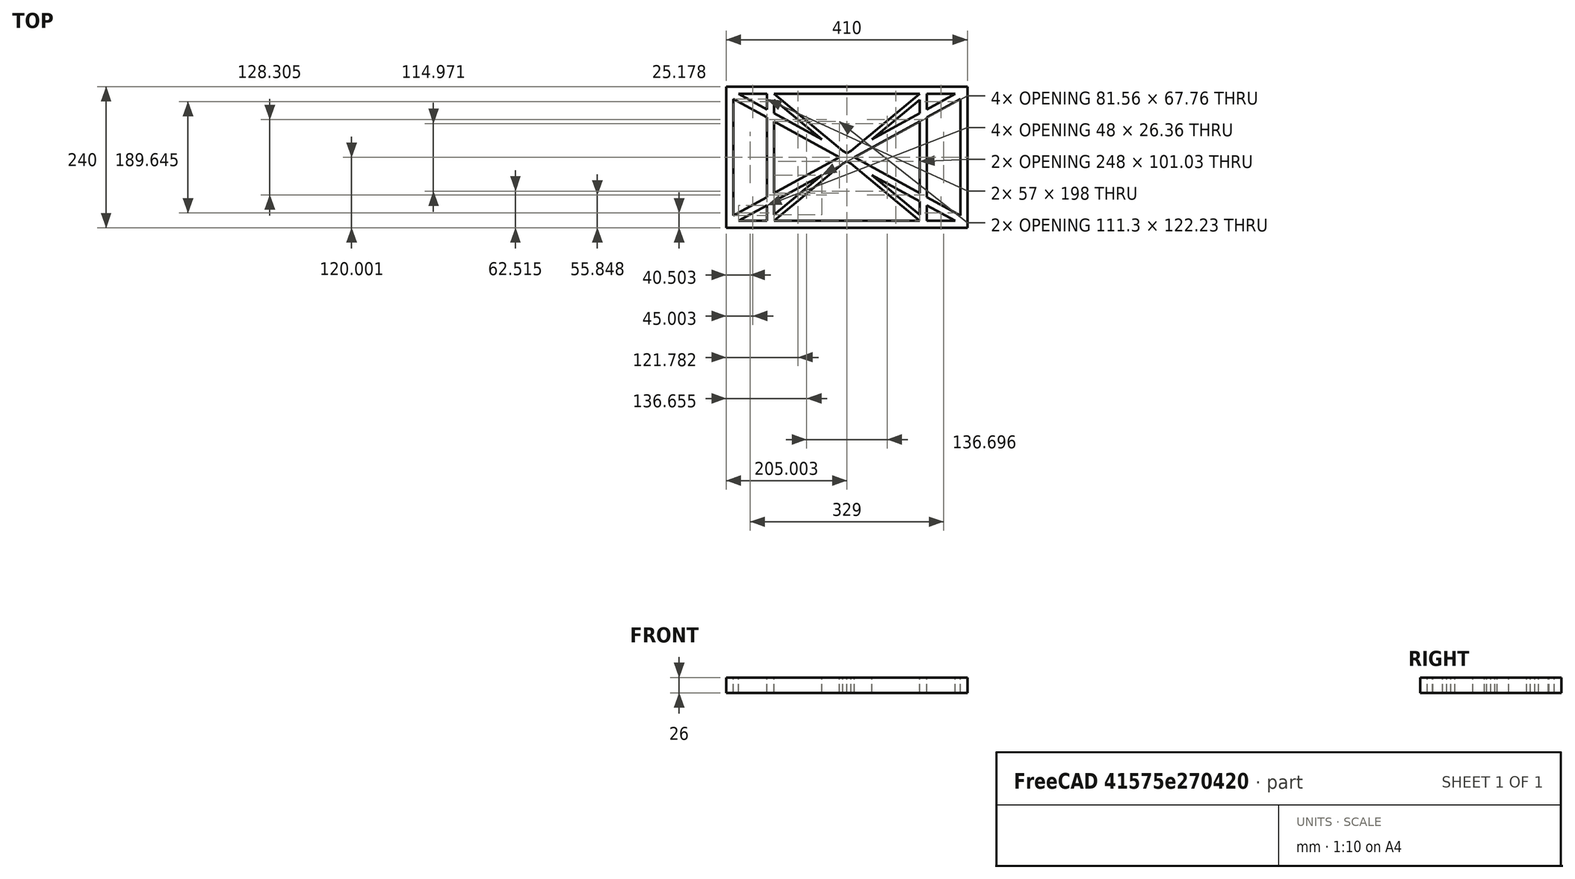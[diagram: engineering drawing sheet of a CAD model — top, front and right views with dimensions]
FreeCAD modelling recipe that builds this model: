
FCSTD DOCUMENT  (FreeCAD 0.19R0.19.2)
Label: laptopStand033
License: All rights reserved
LicenseURL: http://en.wikipedia.org/wiki/All_rights_reserved
objects: Sketcher::SketchObject×3, Part::Extrusion×1
note: 4 computed .brp shape members not serialized (recipe doc carries the construction recipe); baked Part::Feature solids carry a one-line shape summary decoded from their .brp

FEATURE [Sketcher::SketchObject] Sketch
  FullyConstrained = true
  sketch-geometry (52):
    g0: LineSegment StartX=-22.9272 StartY=136.221 StartZ=0 EndX=-22.9272 EndY=-103.779 EndZ=0
    g1: LineSegment StartX=-22.9272 StartY=136.221 StartZ=0 EndX=387.073 EndY=136.221 EndZ=0
    g2: LineSegment StartX=-22.9272 StartY=-103.779 StartZ=0 EndX=387.073 EndY=-103.779 EndZ=0
    g3: LineSegment StartX=387.073 StartY=136.221 StartZ=0 EndX=387.073 EndY=-103.779 EndZ=0
    g4: LineSegment StartX=375.073 StartY=115.221 StartZ=0 EndX=318.073 EndY=83.9235 EndZ=0
    g5: LineSegment StartX=-10.9272 StartY=-82.7794 StartZ=0 EndX=46.0728 EndY=-51.4823 EndZ=0
    g6: LineSegment StartX=-1.92719 StartY=124.221 StartZ=0 EndX=46.0728 EndY=97.8651 EndZ=0
    g7: LineSegment StartX=366.073 StartY=-91.7794 StartZ=0 EndX=318.073 EndY=-65.424 EndZ=0
    g8: LineSegment StartX=-10.9272 StartY=115.221 StartZ=0 EndX=-10.9272 EndY=-82.7794 EndZ=0
    g9: LineSegment StartX=375.073 StartY=-82.7794 StartZ=0 EndX=375.073 EndY=115.221 EndZ=0
    g10: LineSegment StartX=-1.92719 StartY=-91.7794 StartZ=0 EndX=46.0728 EndY=-91.7794 EndZ=0
    g11: LineSegment StartX=318.073 StartY=124.221 StartZ=0 EndX=366.073 EndY=124.221 EndZ=0
    g12: LineSegment StartX=306.073 StartY=-81.8102 StartZ=0 EndX=224.513 EndY=-14.0532 EndZ=0
    g13: LineSegment StartX=58.0728 StartY=114.251 StartZ=0 EndX=139.632 EndY=46.4944 EndZ=0
    g14: LineSegment StartX=306.073 StartY=124.221 StartZ=0 EndX=189.124 EndY=27.0628 EndZ=0
    g15: LineSegment StartX=58.0728 StartY=-91.7794 StartZ=0 EndX=175.022 EndY=5.37834 EndZ=0
    g16: LineSegment StartX=46.0728 StartY=124.221 StartZ=0 EndX=46.0728 EndY=97.8651 EndZ=0
    g17: LineSegment StartX=58.0728 StartY=-81.8102 StartZ=0 EndX=58.0728 EndY=-58.8351 EndZ=0
    g18: LineSegment StartX=318.073 StartY=124.221 StartZ=0 EndX=318.073 EndY=97.8651 EndZ=0
    g19: LineSegment StartX=306.073 StartY=114.251 StartZ=0 EndX=306.073 EndY=91.2763 EndZ=0
    g20: LineSegment StartX=182.073 StartY=23.1914 StartZ=0 EndX=189.124 EndY=27.0628 EndZ=0
    g21: LineSegment StartX=182.073 StartY=9.24976 StartZ=0 EndX=175.022 EndY=5.37834 EndZ=0
    g22: LineSegment StartX=224.513 StartY=46.4944 StartZ=0 EndX=306.073 EndY=114.251 EndZ=0
    g23: LineSegment StartX=175.022 StartY=27.0628 StartZ=0 EndX=58.0728 EndY=124.221 EndZ=0
    g24: LineSegment StartX=169.377 StartY=16.2206 StartZ=0 EndX=58.0728 EndY=77.3346 EndZ=0
    g25: LineSegment StartX=139.632 StartY=-14.0532 StartZ=0 EndX=58.0728 EndY=-81.8102 EndZ=0
    g26: LineSegment StartX=194.768 StartY=16.2206 StartZ=0 EndX=306.073 EndY=-44.8935 EndZ=0
    g27: LineSegment StartX=224.513 StartY=46.4944 StartZ=0 EndX=306.073 EndY=91.2763 EndZ=0
    g28: LineSegment StartX=175.022 StartY=27.0628 StartZ=0 EndX=182.073 EndY=23.1914 EndZ=0
    g29: LineSegment StartX=139.632 StartY=-14.0532 StartZ=0 EndX=58.0728 EndY=-58.8351 EndZ=0
    g30: LineSegment StartX=189.124 StartY=5.37834 StartZ=0 EndX=182.073 EndY=9.24976 EndZ=0
    g31: LineSegment StartX=189.124 StartY=5.37834 StartZ=0 EndX=306.073 EndY=-91.7794 EndZ=0
    g32: LineSegment StartX=306.073 StartY=77.3346 StartZ=0 EndX=306.073 EndY=-44.8935 EndZ=0
    g33: LineSegment StartX=318.073 StartY=83.9235 StartZ=0 EndX=318.073 EndY=-51.4823 EndZ=0
    g34: LineSegment StartX=318.073 StartY=97.8651 StartZ=0 EndX=366.073 EndY=124.221 EndZ=0
    g35: LineSegment StartX=306.073 StartY=77.3346 StartZ=0 EndX=194.768 EndY=16.2206 EndZ=0
    g36: LineSegment StartX=306.073 StartY=-58.8351 StartZ=0 EndX=224.513 EndY=-14.0532 EndZ=0
    g37: LineSegment StartX=306.073 StartY=-58.8351 StartZ=0 EndX=306.073 EndY=-81.8102 EndZ=0
    g38: LineSegment StartX=318.073 StartY=-51.4823 StartZ=0 EndX=375.073 EndY=-82.7794 EndZ=0
    g39: LineSegment StartX=318.073 StartY=-65.424 StartZ=0 EndX=318.073 EndY=-91.7794 EndZ=0
    g40: LineSegment StartX=306.073 StartY=124.221 StartZ=0 EndX=58.0728 EndY=124.221 EndZ=0
    g41: LineSegment StartX=318.073 StartY=-91.7794 StartZ=0 EndX=366.073 EndY=-91.7794 EndZ=0
    g42: LineSegment StartX=58.0728 StartY=-91.7794 StartZ=0 EndX=306.073 EndY=-91.7794 EndZ=0
    g43: LineSegment StartX=58.0728 StartY=-44.8935 StartZ=0 EndX=58.0728 EndY=77.3346 EndZ=0
    g44: LineSegment StartX=46.0728 StartY=-65.424 StartZ=0 EndX=-1.92719 EndY=-91.7794 EndZ=0
    g45: LineSegment StartX=46.0728 StartY=-65.424 StartZ=0 EndX=46.0728 EndY=-91.7794 EndZ=0
    g46: LineSegment StartX=58.0728 StartY=-44.8935 StartZ=0 EndX=169.377 EndY=16.2206 EndZ=0
    g47: LineSegment StartX=58.0728 StartY=91.2763 StartZ=0 EndX=58.0728 EndY=114.251 EndZ=0
    g48: LineSegment StartX=46.0728 StartY=83.9235 StartZ=0 EndX=46.0728 EndY=-51.4823 EndZ=0
    g49: LineSegment StartX=46.0728 StartY=124.221 StartZ=0 EndX=-1.92719 EndY=124.221 EndZ=0
    g50: LineSegment StartX=58.0728 StartY=91.2763 StartZ=0 EndX=139.632 EndY=46.4944 EndZ=0
    g51: LineSegment StartX=46.0728 StartY=83.9235 StartZ=0 EndX=-10.9272 EndY=115.221 EndZ=0
  constraints (102):
    c: Vertical(g0)
    c: Distance(g0) = 240
    c: Horizontal(g1)
    c: Distance(g1) = 410
    c: Coincident(g1,g0)
    c: Coincident(g2,g0)
    c: Horizontal(g2)
    c: Coincident(g3,g1)
    c: Vertical(g3)
    c: Coincident(g2,g3)
    c: Block(g1)
    c: Horizontal(g10)
    c: Horizontal(g11)
    c: PointOnObject(g35,g6)
    c: Coincident(g28,g20)
    c: Coincident(g30,g21)
    c: Tangent(g7,g24)
    c: PointOnObject(g24,g5)
    c: PointOnObject(g26,g4)
    c: Coincident(g20,g14)
    c: Tangent(g20,g27)
    c: Coincident(g50,g13)
    c: Coincident(g28,g23)
    c: Coincident(g22,g27)
    c: Coincident(g21,g15)
    c: Coincident(g29,g25)
    c: Tangent(g21,g29)
    c: Coincident(g36,g12)
    c: Coincident(g31,g30)
    c: Coincident(g22,g19)
    c: Tangent(g19,g32)
    c: Tangent(g18,g33)
    c: Coincident(g27,g19)
    c: Tangent(g27,g34)
    c: Coincident(g4,g33)
    c: Coincident(g35,g32)
    c: Tangent(g4,g35)
    c: Coincident(g37,g12)
    c: Tangent(g7,g36)
    c: Tangent(g32,g37)
    c: Coincident(g26,g32)
    c: Tangent(g26,g38)
    c: Coincident(g33,g38)
    c: Coincident(g39,g7)
    c: Tangent(g33,g39)
    c: Coincident(g25,g17)
    c: Tangent(g17,g43)
    c: Coincident(g29,g17)
    c: Tangent(g29,g44)
    c: Coincident(g45,g44)
    c: Tangent(g16,g45)
    c: Coincident(g5,g48)
    c: Coincident(g46,g43)
    c: Tangent(g5,g46)
    c: Tangent(g43,g47)
    c: Tangent(g16,g48)
    c: Coincident(g13,g47)
    c: PointOnObject(g40,g23)
    c: Tangent(g40,g49)
    c: Coincident(g6,g16)
    c: Coincident(g50,g47)
    c: Tangent(g6,g50)
    c: Coincident(g24,g43)
    c: Coincident(g51,g48)
    c: Tangent(g24,g51)
    c: Block(g23)
    c: Block(g14)
    c: Block(g20)
    c: Block(g40)
    c: Block(g18)
    c: Block(g34)
    c: Block(g4)
    c: Block(g38)
    c: Block(g9)
    c: Block(g36)
    c: Block(g37)
    c: Block(g7)
    c: Block(g39)
    c: Block(g22)
    c: Block(g31)
    c: Block(g42)
    c: Block(g21)
    c: Block(g15)
    c: Block(g29)
    c: Block(g25)
    c: Block(g45)
    c: Block(g44)
    c: Block(g5)
    c: Block(g8)
    c: Block(g51)
    c: Block(g6)
    c: Block(g16)
    c: Block(g13)
    c: Block(g47)
    c: Block(g35)
    c: Block(g32)
    c: Block(g24)
    c: Block(g46)
    c: Block(g49)
    c: Block(g11)
    c: Block(g41)
    c: Block(g10)
FEATURE [Part::Extrusion] Extrude
  Base = -> Sketch
  Dir = (0,0,1)
  DirMode = 2
  FaceMakerClass = Part::FaceMakerBullseye
  LengthFwd = 26
  LengthRev = 0
  Solid = true
  Symmetric = false
FEATURE [Sketcher::SketchObject] Sketch001
  FullyConstrained = true
  MapMode = 4
  Placement = pos=(0,0,0) rot=(0.57735,0.57735,0.57735;2.0944rad)
  Support = -> [Sketch]
  sketch-geometry (46):
    g0: LineSegment StartX=17.2232 StartY=-16.0875 StartZ=0 EndX=117.223 EndY=-16.0875 EndZ=0
    g1: LineSegment StartX=17.2232 StartY=-16.0875 StartZ=0 EndX=17.2232 EndY=-19.0875 EndZ=0
    g2: LineSegment StartX=117.223 StartY=-16.0875 StartZ=0 EndX=117.223 EndY=-19.0875 EndZ=0
    g3: BSplineCurve PolesCount=3 KnotsCount=2 Degree=2 IsPeriodic=0
    g4: LineSegment StartX=17.2232 StartY=-19.0875 StartZ=0 EndX=29.8094 EndY=-19.0875 EndZ=0
    g5: ArcOfCircle CenterX=73.122 CenterY=-32.2909 CenterZ=0 NormalX=0 NormalY=0 NormalZ=1 AngleXU=0 Radius=13 StartAngle=5.92268 EndAngle=9.06428
    g6: LineSegment StartX=85.2864 StartY=-36.8765 StartZ=0 EndX=78.9505 EndY=-53.7246 EndZ=0
    g7: LineSegment StartX=60.9577 StartY=-27.7052 StartZ=0 EndX=54.6191 EndY=-44.5532 EndZ=0
    g8: ArcOfCircle CenterX=66.7816 CenterY=-49.1439 CenterZ=0 NormalX=0 NormalY=0 NormalZ=1 AngleXU=0 Radius=13 StartAngle=2.78068 EndAngle=5.92131
    g9: ArcOfCircle CenterX=55.9263 CenterY=-78.1807 CenterZ=0 NormalX=0 NormalY=0 NormalZ=1 AngleXU=0 Radius=13 StartAngle=5.92268 EndAngle=9.06428
    g10: LineSegment StartX=68.0907 StartY=-82.7664 StartZ=0 EndX=61.7547 EndY=-99.6148 EndZ=0
    g11: ArcOfCircle CenterX=49.5884 CenterY=-95.0342 CenterZ=0 NormalX=0 NormalY=0 NormalZ=1 AngleXU=0 Radius=13 StartAngle=2.78068 EndAngle=5.92131
    g12: LineSegment StartX=43.7619 StartY=-73.595 StartZ=0 EndX=37.426 EndY=-90.4435 EndZ=0
    g13: ArcOfCircle CenterX=38.7206 CenterY=-124.067 CenterZ=0 NormalX=0 NormalY=0 NormalZ=1 AngleXU=0 Radius=13 StartAngle=5.92268 EndAngle=9.06428
    g14: LineSegment StartX=26.5562 StartY=-119.481 StartZ=0 EndX=20.2251 EndY=-136.329 EndZ=0
    g15: ArcOfCircle CenterX=32.3875 CenterY=-140.92 CenterZ=0 NormalX=0 NormalY=0 NormalZ=1 AngleXU=0 Radius=13 StartAngle=2.78068 EndAngle=5.92131
    g16: LineSegment StartX=50.885 StartY=-128.652 StartZ=0 EndX=44.549 EndY=-145.5 EndZ=0
    g17: ArcOfCircle CenterX=21.4715 CenterY=-169.934 CenterZ=0 NormalX=0 NormalY=0 NormalZ=1 AngleXU=0 Radius=13 StartAngle=5.92268 EndAngle=9.06428
    g18: LineSegment StartX=9.3071 StartY=-165.349 StartZ=0 EndX=2.97115 EndY=-182.197 EndZ=0
    g19: ArcOfCircle CenterX=15.1336 CenterY=-186.787 CenterZ=0 NormalX=0 NormalY=0 NormalZ=1 AngleXU=0 Radius=13 StartAngle=2.78068 EndAngle=5.92131
    g20: LineSegment StartX=33.6358 StartY=-174.52 StartZ=0 EndX=27.2999 EndY=-191.368 EndZ=0
    g21: LineSegment StartX=94.6577 StartY=-26.1351 StartZ=0 EndX=25.4551 EndY=-210.153 EndZ=0
    g22-g25: Circle x4 (B-spline internal-alignment scaffolding for g26; pole/knot coordinates omitted)
    g26: BSplineCurve PolesCount=4 KnotsCount=2 Degree=3 IsPeriodic=0
    g27: GeomPoint X=28.8094 Y=-19.0875 Z=0
    g28: GeomPoint X=47.0443 Y=-50.4712 Z=0
    g29: Circle CenterX=53.5586 CenterY=-23.2695 CenterZ=0 NormalX=0 NormalY=0 NormalZ=1 AngleXU=0 Radius=3.24518
    g30: LineSegment StartX=25.4551 StartY=-210.153 StartZ=0 EndX=44.1752 EndY=-217.193 EndZ=0
    g31: LineSegment StartX=44.1752 StartY=-217.193 StartZ=0 EndX=43.1192 EndY=-220.001 EndZ=0
    g32: LineSegment StartX=-195.441 StartY=-127.082 StartZ=0 EndX=-196.497 EndY=-129.89 EndZ=0
    g33: LineSegment StartX=-196.497 StartY=-129.89 StartZ=0 EndX=43.1192 EndY=-220.001 EndZ=0
    g34: LineSegment StartX=12.8789 StartY=-141.321 StartZ=0 EndX=47.0443 EndY=-50.4712 EndZ=0
    g35: Circle CenterX=-195.441 CenterY=-127.082 CenterZ=0 NormalX=0 NormalY=0 NormalZ=1 AngleXU=0 Radius=1
    g36: Circle CenterX=-8.24091 CenterY=-197.481 CenterZ=0 NormalX=0 NormalY=0 NormalZ=1 AngleXU=0 Radius=1
    g37: Circle CenterX=12.8789 CenterY=-141.321 CenterZ=0 NormalX=0 NormalY=0 NormalZ=1 AngleXU=0 Radius=1
    g38: BSplineCurve PolesCount=3 KnotsCount=2 Degree=2 IsPeriodic=0
    g39: GeomPoint X=-195.441 Y=-127.082 Z=0
    g40: GeomPoint X=12.8789 Y=-141.321 Z=0
    g41: Circle CenterX=-12.8016 CenterY=-179.036 CenterZ=0 NormalX=0 NormalY=0 NormalZ=1 AngleXU=0 Radius=10.5072
    g42: Circle CenterX=0.933922 CenterY=-166.43 CenterZ=0 NormalX=0 NormalY=0 NormalZ=1 AngleXU=0 Radius=3.26661
    g43: Circle CenterX=-33.5518 CenterY=-176.44 CenterZ=0 NormalX=0 NormalY=0 NormalZ=1 AngleXU=0 Radius=5.64388
    g44: Circle CenterX=-47.2366 CenterY=-173.859 CenterZ=0 NormalX=0 NormalY=0 NormalZ=1 AngleXU=0 Radius=3.01653
    g45: Circle CenterX=-56.2595 CenterY=-171.456 CenterZ=0 NormalX=0 NormalY=0 NormalZ=1 AngleXU=0 Radius=2.12826
  constraints (82):
    c: Horizontal(g0)
    c: Distance(g0) = 100
    c: Block(g0)
    c: Coincident(g1,g0)
    c: Vertical(g1)
    c: Distance(g1) = 3
    c: Coincident(g2,g0)
    c: Vertical(g2)
    c: Distance(g2) = 3
    c: Block(g3)
    c: Coincident(g3,g2)
    c: Coincident(g4,g1)
    c: Horizontal(g4)
    c: Block(g5)
    c: Distance(g6) = 18
    c: Coincident(g6,g5)
    c: Coincident(g7,g5)
    c: Block(g8)
    c: Coincident(g8,g7)
    c: Block(g7)
    c: Coincident(g10,g9)
    c: Coincident(g12,g9)
    c: Block(g11)
    c: Coincident(g11,g12)
    c: Block(g12)
    c: Block(g9)
    c: Block(g10)
    c: Coincident(g16,g13)
    c: Coincident(g14,g13)
    c: Block(g15)
    c: Coincident(g15,g14)
    c: Block(g14)
    c: Block(g13)
    c: Coincident(g20,g17)
    c: Coincident(g18,g17)
    c: Block(g19)
    c: Coincident(g19,g18)
    c: Block(g18)
    c: Block(g17)
    c: Distance(g20) = 18
    c: Block(g20)
    c: Block(g16)
    c: Coincident(g21,g3)
    c: Block(g21)
    c: Block(g6)
    c: Weight(g22) = 1
    c: Equal(g22,g23)
    c: Equal(g22,g24)
    c: Equal(g22,g25)
    c: InternalAlignment(g22-g25 -> g26) x4
    c: InternalAlignment(g27,g26)
    c: InternalAlignment(g28,g26)
    c: PointOnObject(g4,g22)
    c: Block(g26)
    c: Block(g29)
    c: Distance(g30) = 20
    c: Perpendicular(g21,g30)
    c: Coincident(g30,g21)
    c: Distance(g31) = 3
    c: Perpendicular(g30,g31)
    c: Distance(g32) = 3
    c: Coincident(g33,g32)
    c: Coincident(g33,g31)
    c: Block(g33)
    c: Block(g32)
    c: Coincident(g34,g26)
    c: Block(g31)
    c: Weight(g35) = 1
    c: Equal(g35,g36)
    c: Equal(g35,g37)
    c: InternalAlignment(g35,g38)
    c: InternalAlignment(g36,g38)
    c: InternalAlignment(g37,g38)
    c: InternalAlignment(g39,g38)
    c: InternalAlignment(g40,g38)
    c: Block(g38)
    c: Block(g34)
    c: Block(g41)
    c: Block(g42)
    c: Block(g43)
    c: Block(g44)
    c: Block(g45)
FEATURE [Sketcher::SketchObject] Sketch002
  FullyConstrained = true
  Placement = pos=(0,0,0) rot=(-1,0,0;4.71239rad)
